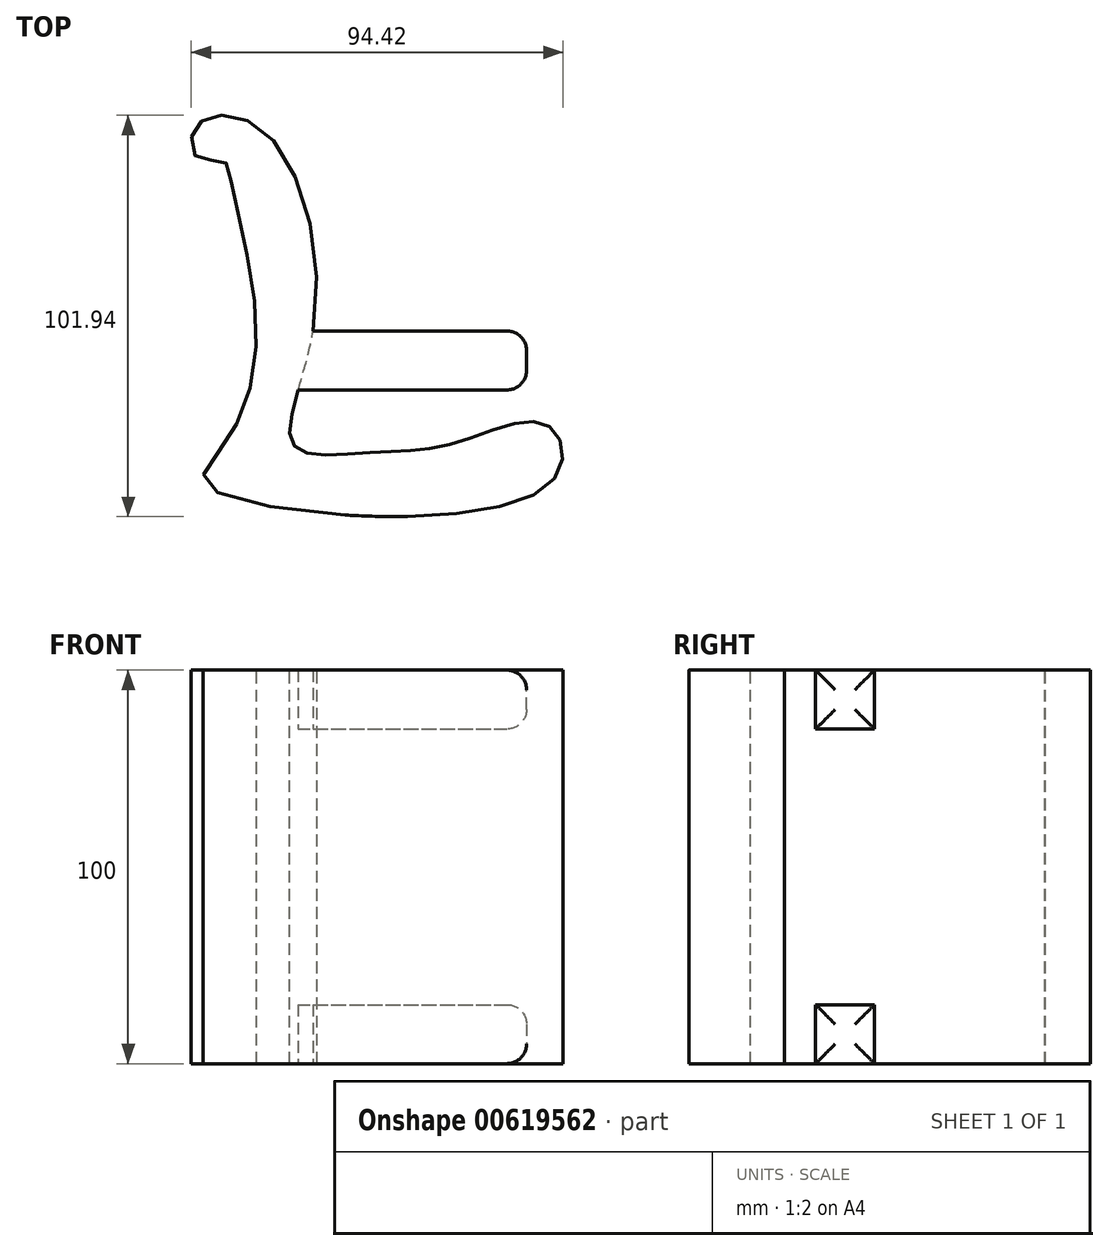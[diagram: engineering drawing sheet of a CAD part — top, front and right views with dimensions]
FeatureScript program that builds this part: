
annotation { "Feature Type Name" : "Feature", "Feature Type Description" : "" }
export const myFeature = defineFeature(function(context is Context, id is Id, definition is map)
    precondition{}
    {
        {
            var Q0;
            Q0=qCreatedBy(makeId("Top.planeOp"),FACE);
            var sketch = newSketch(context, id + "F0", { "sketchPlane" : qUnion([Q0])});
            skFitSpline(sketch, "E0", {"points": [v(-42.35, 58.56) * mm, v(-47.86, 54.15) * mm, v(-46.31, 47.79) * mm, v(-40.1, 47.23) * mm, v(-37.88, 41.03) * mm, v(-31.59, 4.54) * mm, v(-40.08, -25.3) * mm, v(-44.07, -35.35) * mm, v(41.64, -36) * mm, v(42.3, -19.92) * mm, v(19.32, -24.36) * mm, v(-2.67, -26.88) * mm, v(-22.18, -25) * mm, v(-16.8, 6.75) * mm, v(-28.09, 53.25) * mm, v(-42.35, 58.56) * mm]});
            skFitSpline(sketch, "E1", {"points": [v(-9.04, -42.77) * mm, v(-8.87, -63.35) * mm, v(-38.86, -71.12) * mm, v(-40.41, -74.23) * mm, v(0, -75.57) * mm, v(38.45, -73.79) * mm, v(37.34, -69.8) * mm, v(6.9, -65.13) * mm, v(6.75, -43.13) * mm], "startDerivative": vector(68.9, -214.07) * mm, "endDerivative": vector(68.5, 227.01) * mm});
            skSolve(sketch);
        }
        {
            var Q0;
            Q0=makeQuery(id+"F0.imprint","IMPRINT",FACE,{"disambiguationData":[TD([[makeQuery(id+"F0.imprint","IMPRINT",EDGE,{"derivedFrom":sQuery(id+"F0.wireOp",EDGE,"E0")}),1.0]])]});
            extrude(context, id + "F1", {"entities" : qUnion([Q0]), "depth" : 100 * mm, "offsetDistance" : 25.4 * mm});
        }
        {
            var Q0;
            Q0=qCreatedBy(makeId("Top.planeOp"),FACE);
            cPlane(context, id + "F2", {"entities" : qUnion([Q0]), "cplaneType" : CPlaneType.OFFSET, "offset" : 50 * mm, "width" : 150 * mm, "height" : 150 * mm});
        }
        {
            var Q0;
            Q0=qCreatedBy(makeId("Top.planeOp"),FACE);
            var sketch = newSketch(context, id + "F3", { "sketchPlane" : qUnion([Q0])});
            skLineSegment(sketch, "E2.bottom", {"start": v(-23, 4.01) * mm, "end": v(37, 4.01) * mm});
            skLineSegment(sketch, "E2.top", {"start": v(-23, -10.99) * mm, "end": v(37, -10.99) * mm});
            skLineSegment(sketch, "E2.left", {"start": v(-23, 4.01) * mm, "end": v(-23, -10.99) * mm});
            skLineSegment(sketch, "E2.right", {"start": v(37, 4.01) * mm, "end": v(37, -10.99) * mm});
            skSolve(sketch);
        }
        {
            var Q0;
            Q0=makeQuery(id+"F3.imprint","IMPRINT",FACE,{"disambiguationData":[TD([[makeQuery(id+"F3.imprint","IMPRINT",EDGE,{"derivedFrom":sQuery(id+"F3.wireOp",EDGE,"E2.bottom")}),-1.0]])]});
            extrude(context, id + "F4", {"entities" : qUnion([Q0]), "depth" : 15 * mm, "offsetDistance" : 25 * mm});
        }
        {
            var Q0;
            Q0=makeQuery(id+"F4.opExtrude","SWEPT_BODY",BODY,{"disambiguationData":[OSD([sQuery(id+"F3.wireOp",EDGE,"E2.bottom"),sQuery(id+"F3.wireOp",EDGE,"E2.top"),sQuery(id+"F3.wireOp",EDGE,"E2.left"),sQuery(id+"F3.wireOp",EDGE,"E2.right")])]});
            var Q1;
            Q1=qCreatedBy(id+"F2.planeOp",FACE);
            mirror(context, id + "F5", {"operationType" : NewBodyOperationType.ADD, "entities" : qUnion([Q0]), "mirrorPlane" : qUnion([Q1])});
        }
        {
            var Q0;
            Q0=makeQuery(id+"F5.opPattern","COPY",FACE,{"derivedFrom":makeQuery(id+"F4.opExtrude","SWEPT_FACE",FACE,{"disambiguationData":[OSD([sQuery(id+"F3.wireOp",EDGE,"E2.right")])]}),"instanceName":"1"});
            fillet(context, id + "F6", {"entities" : qUnion([Q0]), "radius" : 5 * mm, "tangentPropagation" : true, "allowEdgeOverflow" : false});
        }
        {
            var Q0;
            Q0=makeQuery(id+"F4.opExtrude","SWEPT_FACE",FACE,{"disambiguationData":[OSD([sQuery(id+"F3.wireOp",EDGE,"E2.right")])]});
            fillet(context, id + "F7", {"entities" : qUnion([Q0]), "radius" : 5 * mm, "tangentPropagation" : true, "allowEdgeOverflow" : false});
        }
    });
